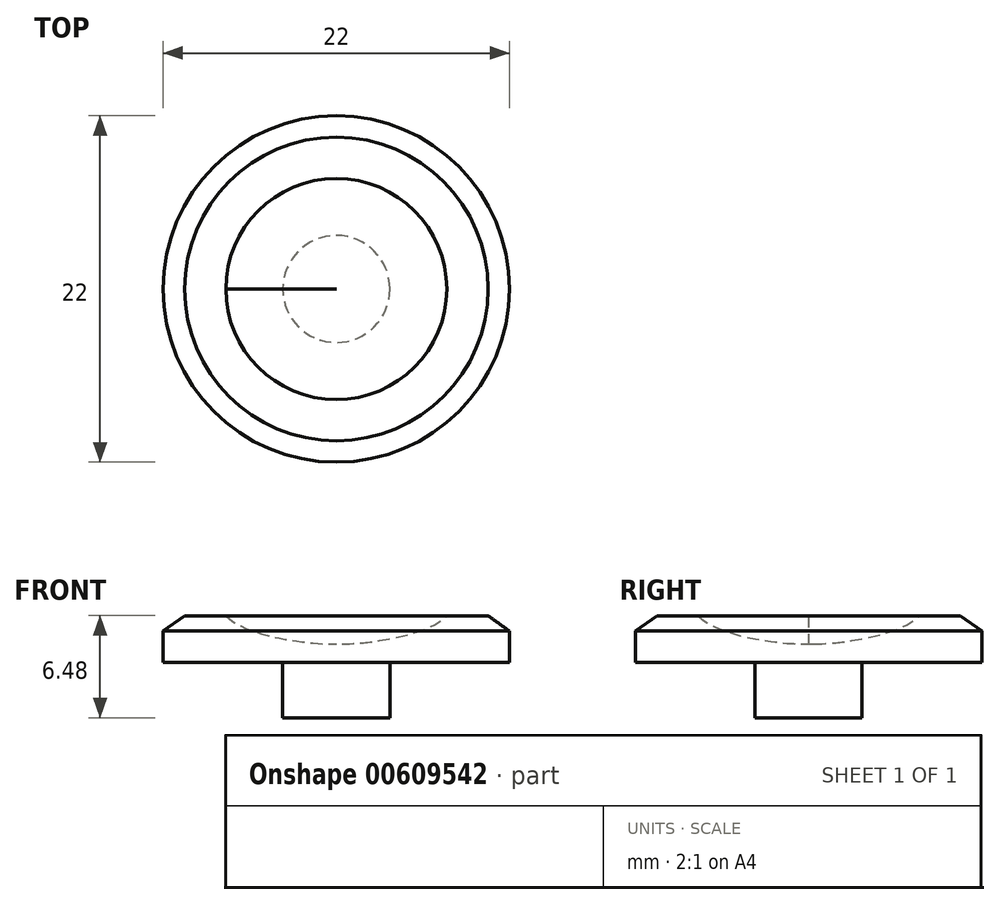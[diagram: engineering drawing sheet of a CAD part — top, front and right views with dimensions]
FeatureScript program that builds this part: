
annotation { "Feature Type Name" : "Feature", "Feature Type Description" : "" }
export const myFeature = defineFeature(function(context is Context, id is Id, definition is map)
    precondition{}
    {
        {
            var Q0;
            Q0=qCreatedBy(makeId("Front.planeOp"),FACE);
            var sketch = newSketch(context, id + "F0", { "sketchPlane" : qUnion([Q0])});
            skLineSegment(sketch, "E0", {"start": v(0, 0) * mm, "end": v(-11, 0) * mm});
            skLineSegment(sketch, "E1", {"start": v(-11, 0) * mm, "end": v(-11, 2) * mm});
            skLineSegment(sketch, "E2", {"start": v(-11, 2) * mm, "end": v(-9.64, 2.98) * mm});
            skLineSegment(sketch, "E3", {"start": v(-9.64, 2.98) * mm, "end": v(-7.02, 2.98) * mm});
            skLineSegment(sketch, "E4", {"start": v(0, 0) * mm, "end": v(0, 1.2) * mm});
            skFitSpline(sketch, "E5", {"points": [v(-7.02, 2.98) * mm, v(0, 1.2) * mm], "startDerivative": vector(4.07, -4.3) * mm, "endDerivative": vector(3.55, 0.28) * mm});
            skLineSegment(sketch, "E6", {"start": v(0, 0) * mm, "end": v(0, -3.5) * mm});
            skLineSegment(sketch, "E7", {"start": v(0, -3.5) * mm, "end": v(-3.4, -3.5) * mm});
            skLineSegment(sketch, "E8", {"start": v(-3.4, -3.5) * mm, "end": v(-3.4, 0) * mm});
            skPoint(sketch, "E9.endSnap0", {"position": v(-3.4, -1.75) * mm});
            skLineSegment(sketch, "E10", {"start": v(-4.55, 0) * mm, "end": v(-4.55, 0) * mm});
            skLineSegment(sketch, "E11", {"start": v(-4.55, 0) * mm, "end": v(-3.4, 0) * mm});
            skSolve(sketch);
        }
        {
            var Q0;
            {var subQ0=sQuery(id+"F0.wireOp",EDGE,"E1");Q0=makeQuery(id+"F0.imprint","IMPRINT",FACE,{"disambiguationData":[TD([[makeQuery(id+"F0.imprint","IMPRINT",EDGE,{"derivedFrom":subQ0}),-1.0]])]});}
            var Q1;
            {var subQ0=sQuery(id+"F0.wireOp",EDGE,"E6");Q1=makeQuery(id+"F0.imprint","IMPRINT",FACE,{"disambiguationData":[TD([[makeQuery(id+"F0.imprint","IMPRINT",EDGE,{"derivedFrom":subQ0}),-1.0]])]});}
            var Q2;
            Q2=sQuery(id+"F0.wireOp",EDGE,"E6");
            revolve(context, id + "F1", {"entities" : qUnion([Q0, Q1]), "axis" : qUnion([Q2]), "revolveType" : RevolveType.FULL});
        }
    });
